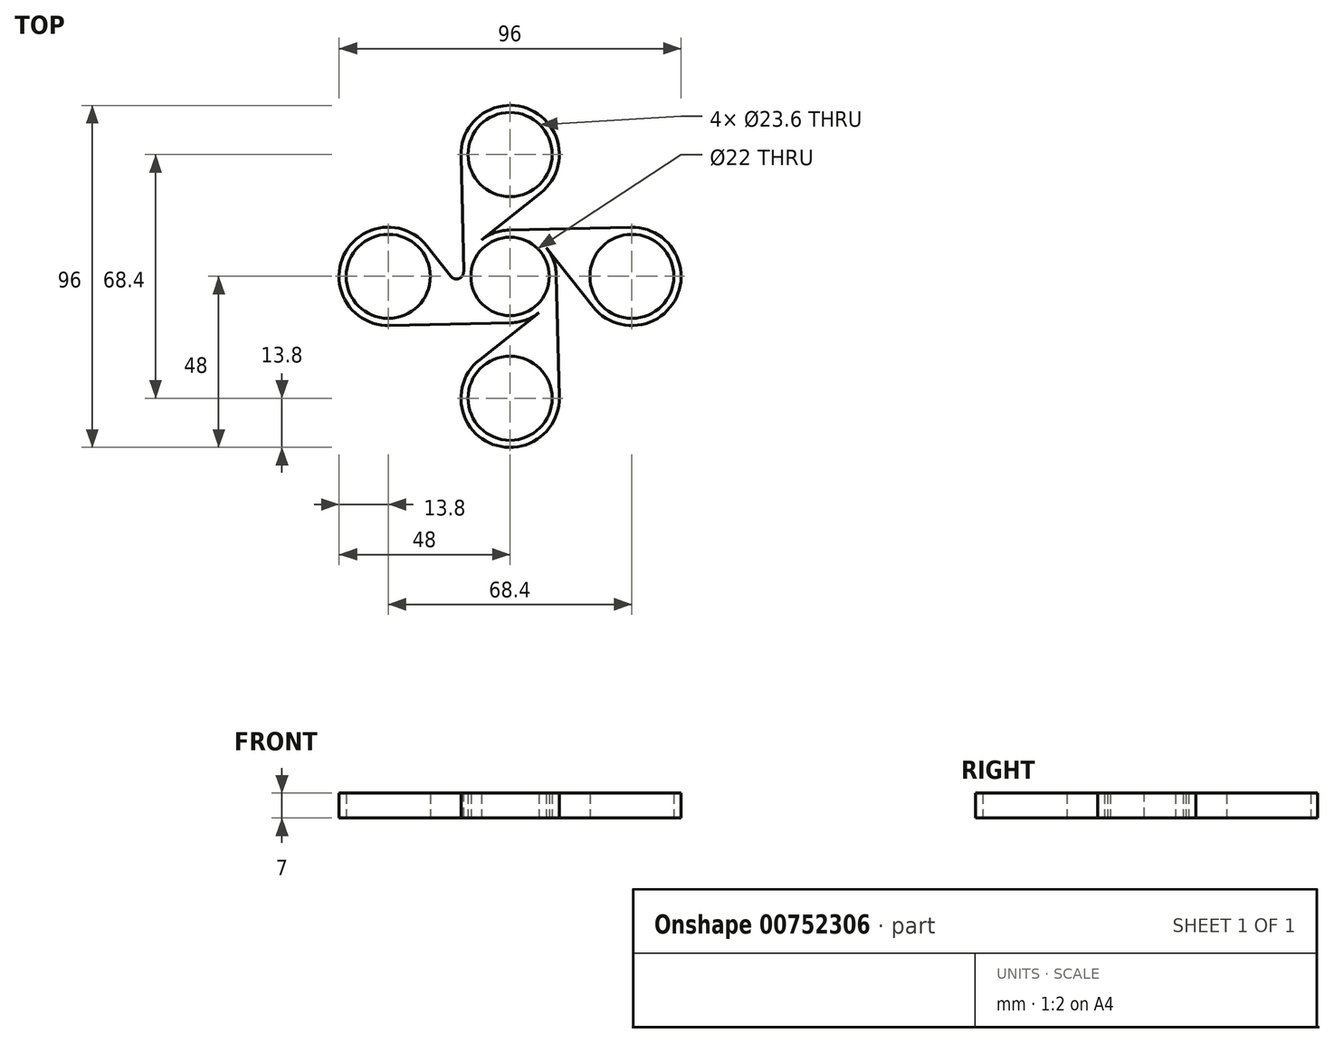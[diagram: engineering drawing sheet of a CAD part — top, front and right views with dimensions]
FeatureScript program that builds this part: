
annotation { "Feature Type Name" : "Feature", "Feature Type Description" : "" }
export const myFeature = defineFeature(function(context is Context, id is Id, definition is map)
    precondition{}
    {
        {
            var Q0;
            Q0=qCreatedBy(makeId("Top.planeOp"),FACE);
            var sketch = newSketch(context, id + "F0", { "sketchPlane" : qUnion([Q0])});
            skCircle(sketch, "E0", {"center": v(0, 0) * mm, "radius": 11 * mm});
            skCircle(sketch, "E1", {"center": v(0, 0) * mm, "radius": 48 * mm});
            skCircle(sketch, "E2", {"center": v(0, 0) * mm, "radius": 46 * mm});
            skCircle(sketch, "E3", {"center": v(-34.2, 0) * mm, "radius": 11.8 * mm});
            skCircle(sketch, "E4", {"center": v(0, 34.2) * mm, "radius": 11.8 * mm});
            skCircle(sketch, "E5", {"center": v(34.2, 0) * mm, "radius": 11.8 * mm});
            skCircle(sketch, "E6", {"center": v(0, -34.2) * mm, "radius": 11.8 * mm});
            skLineSegment(sketch, "E7", {"start": v(0, 0) * mm, "end": v(0, 34.2) * mm});
            skLineSegment(sketch, "E8", {"start": v(34.2, 0) * mm, "end": v(0, 0) * mm});
            skLineSegment(sketch, "E9", {"start": v(0, -34.2) * mm, "end": v(0, 0) * mm});
            skLineSegment(sketch, "E10", {"start": v(-34.2, 0) * mm, "end": v(0, 0) * mm});
            skCircle(sketch, "E11", {"center": v(-34.2, 0) * mm, "radius": 11 * mm});
            skCircle(sketch, "E12", {"center": v(0, 34.2) * mm, "radius": 11 * mm});
            skCircle(sketch, "E13", {"center": v(34.2, 0) * mm, "radius": 11 * mm});
            skCircle(sketch, "E14", {"center": v(0, -34.2) * mm, "radius": 11 * mm});
            skCircle(sketch, "E15", {"center": v(-34.2, 0) * mm, "radius": 13.8 * mm});
            skCircle(sketch, "E16", {"center": v(0, 34.2) * mm, "radius": 13.8 * mm});
            skCircle(sketch, "E17", {"center": v(34.2, 0) * mm, "radius": 13.8 * mm});
            skCircle(sketch, "E18", {"center": v(0, -34.2) * mm, "radius": 13.8 * mm});
            skCircle(sketch, "E19", {"center": v(-18.78, 18.78) * mm, "radius": 10.5 * mm});
            skCircle(sketch, "E20.MirrorC", {"center": v(18.78, 18.78) * mm, "radius": 10.5 * mm});
            skCircle(sketch, "E21.MirrorC", {"center": v(-18.78, -18.78) * mm, "radius": 10.5 * mm});
            skCircle(sketch, "E22.MirrorC", {"center": v(18.78, -18.78) * mm, "radius": 10.5 * mm});
            skSolve(sketch);
        }
        {
            var Q0;
            Q0=qCreatedBy(makeId("Top.planeOp"),FACE);
            var sketch = newSketch(context, id + "F1", { "sketchPlane" : qUnion([Q0])});
            skCircle(sketch, "E23.0", {"center": v(-34.2, 0) * mm, "radius": 13.8 * mm});
            skCircle(sketch, "E23.1", {"center": v(-34.2, 0) * mm, "radius": 11.8 * mm});
            skCircle(sketch, "E23.2", {"center": v(0, 0) * mm, "radius": 11 * mm});
            skCircle(sketch, "E24", {"center": v(0, 0) * mm, "radius": 13 * mm});
            skLineSegment(sketch, "E25", {"start": v(0.3, -13) * mm, "end": v(-33.88, -13.8) * mm});
            skLineSegment(sketch, "E26", {"start": v(-23.39, 8.57) * mm, "end": v(-10.19, -8.08) * mm});
            skSolve(sketch);
        }
        {
            var Q0;
            Q0 = qSketchRegion(id + "F1", true);
            extrude(context, id + "F2", {"entities" : qUnion([Q0]), "depth" : 7 * mm, "offsetDistance" : 25 * mm});
        }
        {
            var Q0;
            Q0=makeQuery(id+"F2.opExtrude","SWEPT_BODY",BODY,{"disambiguationData":[OSD([sQuery(id+"F1.wireOp",EDGE,"E23.0"),sQuery(id+"F1.wireOp",EDGE,"E23.1"),sQuery(id+"F1.wireOp",EDGE,"E23.2"),sQuery(id+"F1.wireOp",EDGE,"E24"),sQuery(id+"F1.wireOp",EDGE,"E25"),sQuery(id+"F1.wireOp",EDGE,"E26")])]});
            var Q1;
            Q1=sQuery(id+"F0.wireOp",EDGE,"E0");
            circularPattern(context, id + "F3", {"operationType" : NewBodyOperationType.ADD, "entities" : qUnion([Q0]), "axis" : qUnion([Q1]), "angle" : 360 * degree, "instanceCount" : 4, "equalSpace" : true});
        }
        {
            var Q0;
            Q0=makeQuery(id+"F2.opExtrude","SWEPT_EDGE",EDGE,{"disambiguationData":[OSD([sQuery(id+"F1.wireOp",EDGE,"E24"),sQuery(id+"F1.wireOp",EDGE,"E26")])]});
            var Q1;
            {var subQ0=makeQuery(id+"F2.opExtrude","SWEPT_FACE",FACE,{"disambiguationData":[OSD([sQuery(id+"F1.wireOp",EDGE,"E24")])]});Q1=makeQuery(id+"F3.boolean.opBoolean","INTERSECT",EDGE,{"disambiguationData":[topologyDisambiguationEdgeConnected([makeQuery(id+"F3.opPattern","COPY",FACE,{"derivedFrom":makeQuery(id+"F2.opExtrude","SWEPT_FACE",FACE,{"disambiguationData":[OSD([sQuery(id+"F1.wireOp",EDGE,"E26")])]}),"instanceName":"3"})])],"derivedFrom":[makeQuery(id+"F3.opPattern","COPY",FACE,{"derivedFrom":subQ0,"instanceName":"1"}),makeQuery(id+"F3.opPattern","COPY",FACE,{"derivedFrom":subQ0,"instanceName":"2"})]});}
            var Q2;
            {var subQ0=makeQuery(id+"F2.opExtrude","SWEPT_FACE",FACE,{"disambiguationData":[OSD([sQuery(id+"F1.wireOp",EDGE,"E24")])]});Q2=makeQuery(id+"F3.boolean.opBoolean","INTERSECT",EDGE,{"disambiguationData":[topologyDisambiguationEdgeConnected([makeQuery(id+"F3.opPattern","COPY",FACE,{"derivedFrom":makeQuery(id+"F2.opExtrude","SWEPT_FACE",FACE,{"disambiguationData":[OSD([sQuery(id+"F1.wireOp",EDGE,"E26")])]}),"instanceName":"2"})])],"derivedFrom":[makeQuery(id+"F3.opPattern","COPY",FACE,{"derivedFrom":subQ0,"instanceName":"1"}),makeQuery(id+"F3.opPattern","COPY",FACE,{"derivedFrom":subQ0,"instanceName":"3"})]});}
            var Q3;
            Q3=makeQuery(id+"F3.opPattern","COPY",EDGE,{"derivedFrom":makeQuery(id+"F2.opExtrude","SWEPT_EDGE",EDGE,{"disambiguationData":[OSD([sQuery(id+"F1.wireOp",EDGE,"E24"),sQuery(id+"F1.wireOp",EDGE,"E26")])]}),"instanceName":"1"});
            fillet(context, id + "F4", {"entities" : qUnion([Q0, Q1, Q2, Q3]), "radius" : 2 * mm, "tangentPropagation" : true, "allowEdgeOverflow" : false});
        }
    });
